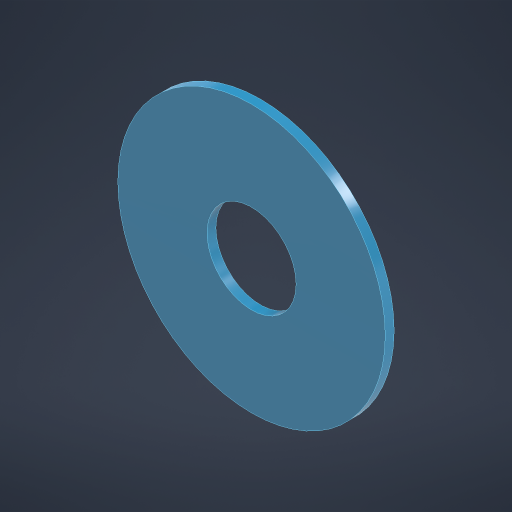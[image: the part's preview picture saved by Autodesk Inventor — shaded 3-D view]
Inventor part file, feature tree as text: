
AUTODESK INVENTOR PART (.ipt)
format: ipt  version: 2023 (Build 270158000, 158)  size: 173,056 bytes
history: native  units: mm
features: sketch x2, extrude x1, hole x1
ambient origin geometry x8: Origin, YZ Plane, XZ Plane, XY Plane, X Axis, Y Axis, Z Axis, Center Point
bodies: Solid1 (feature_tree)
feature tree (4):
  extrude  "Extrusion1"  Depth=1.0mm TaperAngle=0.0deg
  hole  "Hole1"  [1 undecoded]
  sketch  "Sketch1"  dims[d0=30.0mm d1=1.0mm d2=0.0mm]
  sketch  "Sketch2"  dims[d3=10.0mm d4=6.0mm d5=4.0mm d6=2.0mm d7=90.0deg d8=4.0mm d9=0.0mm]
note: 1 required parameter value undecoded (feature->parameter linkage not recoverable at this tier; creation-order binding heuristic only, values carry confidence <= 0.55)
